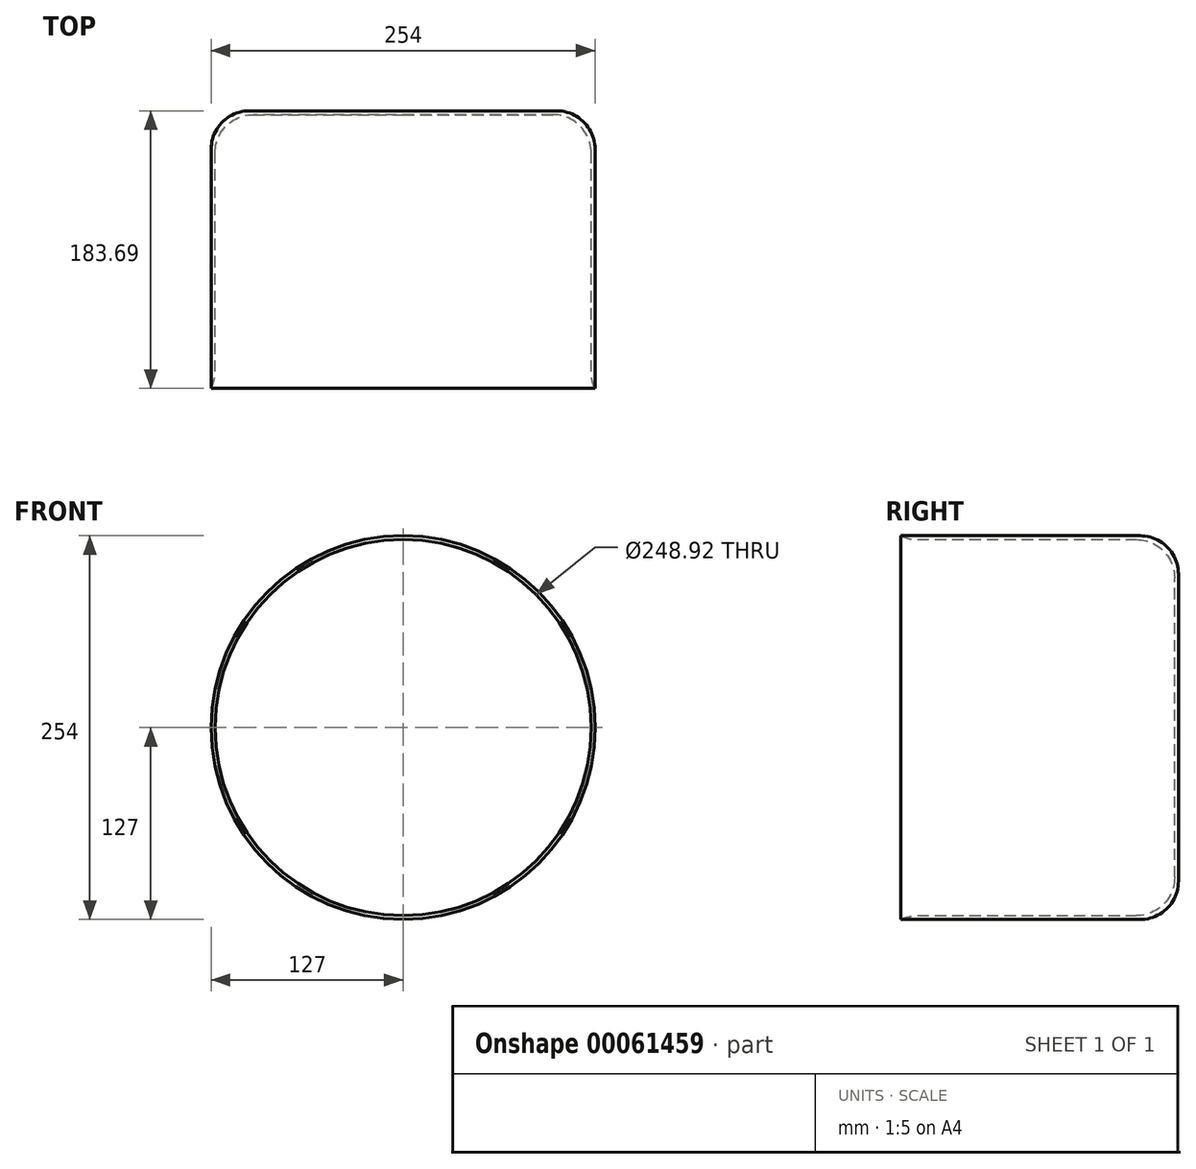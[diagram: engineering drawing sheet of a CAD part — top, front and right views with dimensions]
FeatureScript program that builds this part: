
annotation { "Feature Type Name" : "Feature", "Feature Type Description" : "" }
export const myFeature = defineFeature(function(context is Context, id is Id, definition is map)
    precondition{}
    {
        {
            var Q0;
            Q0=qCreatedBy(makeId("Front.planeOp"),FACE);
            var sketch = newSketch(context, id + "F0", { "sketchPlane" : qUnion([Q0])});
            skCircle(sketch, "E0", {"center": v(0, 0) * mm, "radius": 127 * mm});
            skSolve(sketch);
        }
        {
            var Q0;
            Q0=makeQuery(id+"F0.imprint","IMPRINT",FACE,{"disambiguationData":[TD([[makeQuery(id+"F0.imprint","IMPRINT",EDGE,{"derivedFrom":sQuery(id+"F0.wireOp",EDGE,"E0")}),1.0]])]});
            extrude(context, id + "F1", {"entities" : qUnion([Q0]), "depth" : 183.7 * mm});
        }
        {
            var Q0;
            Q0=makeQuery(id+"F1.opExtrude","CAP_FACE",FACE,{"disambiguationData":[OSD([sQuery(id+"F0.wireOp",EDGE,"E0")])],"isStart":false});
            shell(context, id + "F2", {"entities" : qUnion([Q0]), "thickness" : 2.54 * mm});
        }
        {
            var Q0;
            Q0=makeQuery(id+"F1.opExtrude","CAP_FACE",FACE,{"disambiguationData":[OSD([sQuery(id+"F0.wireOp",EDGE,"E0")])],"isStart":true});
            var Q1;
            Q1=makeQuery(id+"F1.opExtrude","CAP_EDGE",EDGE,{"disambiguationData":[OSD([sQuery(id+"F0.wireOp",EDGE,"E0")])],"isStart":true});
            var Q2;
            {var subQ0=sQuery(id+"F0.wireOp",EDGE,"E0");Q2=makeQuery(id+"F2.opShell","OFFSET_EDGE",EDGE,{"disambiguationData":[OSD([subQ0]),TDD([makeQuery(id+"F1.opExtrude","CAP_EDGE",EDGE,{"disambiguationData":[OSD([subQ0])],"isStart":true})])]});}
            var Q3;
            {var subQ0=sQuery(id+"F0.wireOp",EDGE,"E0");Q3=makeQuery(id+"F2.opShell","OFFSET_FACE",FACE,{"disambiguationData":[OSD([subQ0]),TDD([makeQuery(id+"F1.opExtrude","CAP_FACE",FACE,{"disambiguationData":[OSD([subQ0])],"isStart":true})])]});}
            var Q4;
            {var subQ0=sQuery(id+"F0.wireOp",EDGE,"E0");Q4=makeQuery(id+"F2.opShell","OFFSET_EDGE",EDGE,{"disambiguationData":[OSD([subQ0]),TDD([makeQuery(id+"F1.opExtrude","CAP_EDGE",EDGE,{"disambiguationData":[OSD([subQ0])],"isStart":false})])]});}
            fillet(context, id + "F3", {"entities" : qUnion([Q0, Q1, Q2, Q3, Q4]), "radius" : 25.4 * mm, "tangentPropagation" : true, "allowEdgeOverflow" : false});
        }
    });
